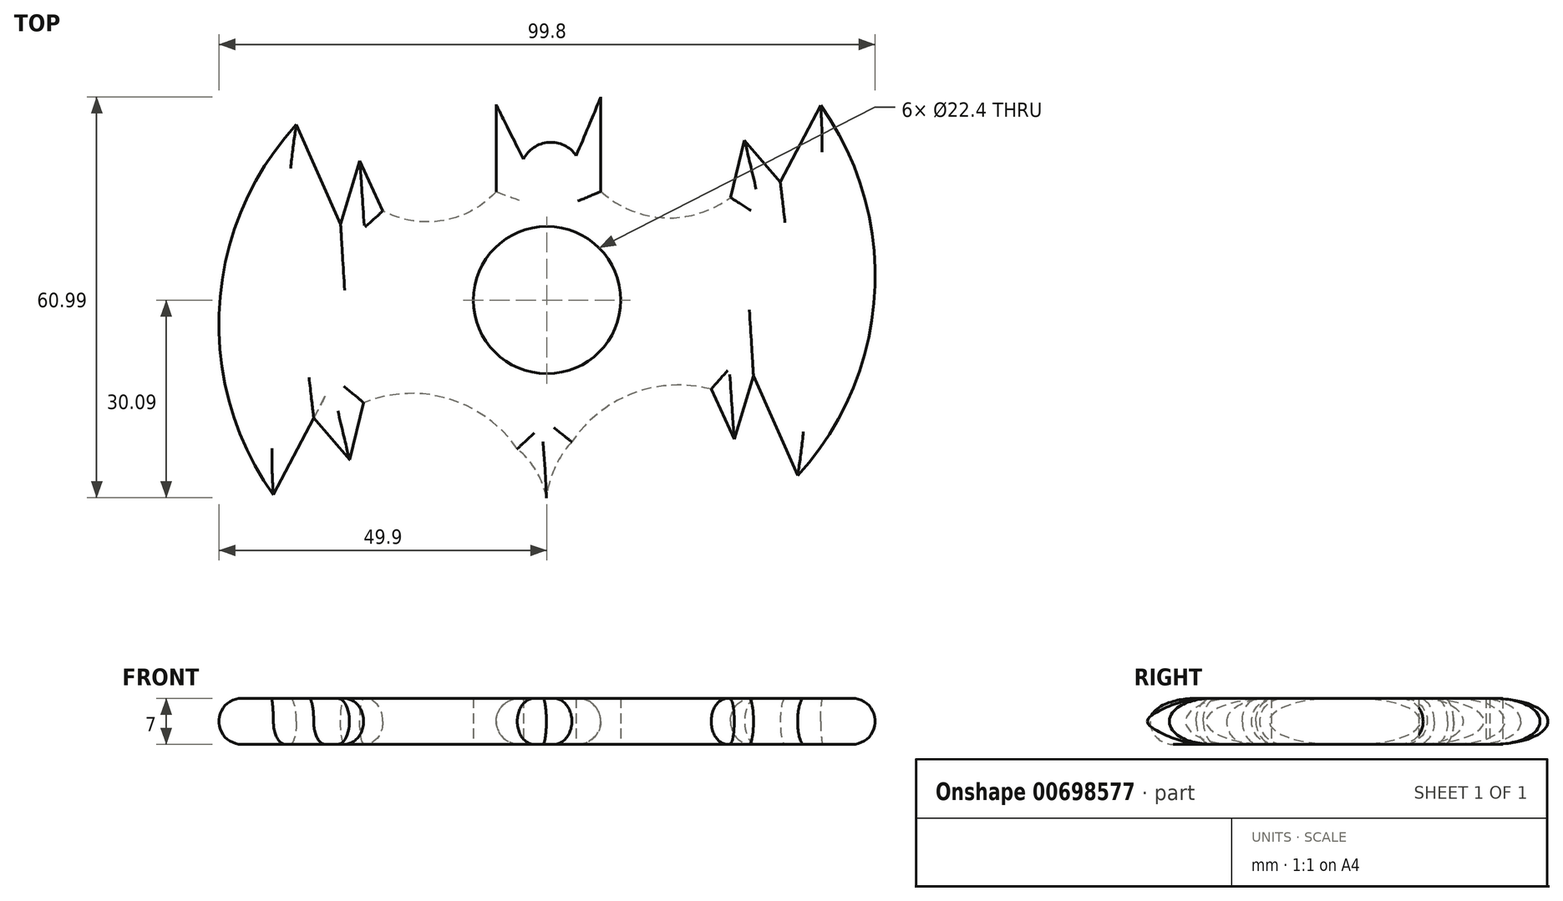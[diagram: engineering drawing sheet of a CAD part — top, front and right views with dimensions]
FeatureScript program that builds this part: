
annotation { "Feature Type Name" : "Feature", "Feature Type Description" : "" }
export const myFeature = defineFeature(function(context is Context, id is Id, definition is map)
    precondition{}
    {
        {
            var Q0;
            Q0=qCreatedBy(makeId("Top.planeOp"),FACE);
            var sketch = newSketch(context, id + "F0", { "sketchPlane" : qUnion([Q0])});
            skCircle(sketch, "E0", {"center": v(0, 0) * mm, "radius": 11.2 * mm});
            skCircle(sketch, "E1", {"center": v(0, 0) * mm, "radius": 13.2 * mm});
            skArc(sketch, "E2", {"start": v(-38.1, 26.72) * mm, "mid": v(-49.82, -0.84) * mm, "end": v(-41.61, -29.64) * mm});
            skArc(sketch, "E3.1.0", {"start": v(38.1, -26.72) * mm, "mid": v(49.82, 0.84) * mm, "end": v(41.61, 29.64) * mm});
            skLineSegment(sketch, "E4", {"start": v(-41.61, -29.64) * mm, "end": v(-35.48, -17.96) * mm});
            skLineSegment(sketch, "E5", {"start": v(-35.48, -17.96) * mm, "end": v(-35.48, -24.97) * mm});
            skArc(sketch, "E6", {"start": v(-4.53, -22.63) * mm, "mid": v(-14.98, -15.03) * mm, "end": v(-27.89, -15.62) * mm});
            skLineSegment(sketch, "E7.1.0", {"start": v(41.61, 29.64) * mm, "end": v(35.48, 17.96) * mm});
            skLineSegment(sketch, "E7.1.1", {"start": v(35.48, 17.96) * mm, "end": v(30.03, 24.29) * mm});
            skLineSegment(sketch, "E7.1.2", {"start": v(30.03, 24.29) * mm, "end": v(27.89, 15.62) * mm});
            skLineSegment(sketch, "E8", {"start": v(38.1, -26.72) * mm, "end": v(31.4, -11.53) * mm});
            skLineSegment(sketch, "E9", {"start": v(31.4, -11.53) * mm, "end": v(28.47, -21.17) * mm});
            skLineSegment(sketch, "E10", {"start": v(28.47, -21.17) * mm, "end": v(24.97, -13.58) * mm});
            skArc(sketch, "E11.1.0", {"start": v(-24.97, 13.58) * mm, "mid": v(-15.85, 12.08) * mm, "end": v(-7.74, 16.5) * mm});
            skLineSegment(sketch, "E11.1.2", {"start": v(-28.47, 21.17) * mm, "end": v(-24.97, 13.58) * mm});
            skLineSegment(sketch, "E11.1.4", {"start": v(-31.4, 11.53) * mm, "end": v(-28.47, 21.17) * mm});
            skLineSegment(sketch, "E11.1.5", {"start": v(-38.1, 26.72) * mm, "end": v(-31.4, 11.53) * mm});
            skArc(sketch, "E12", {"start": v(0, -34.06) * mm, "mid": v(-0.76, -27.75) * mm, "end": v(-4.53, -22.63) * mm});
            skArc(sketch, "E13.1.0", {"start": v(8.2, 16.53) * mm, "mid": v(17.88, 12.52) * mm, "end": v(27.89, 15.62) * mm});
            skLineSegment(sketch, "E14", {"start": v(-7.74, 16.5) * mm, "end": v(-7.74, 29.75) * mm});
            skLineSegment(sketch, "E15", {"start": v(-7.74, 29.75) * mm, "end": v(-3.6, 21.41) * mm});
            skLineSegment(sketch, "E16", {"start": v(8.2, 16.53) * mm, "end": v(8.2, 30.9) * mm});
            skLineSegment(sketch, "E17", {"start": v(8.2, 30.9) * mm, "end": v(4.45, 21.97) * mm});
            skArc(sketch, "E18", {"start": v(4.45, 21.97) * mm, "mid": v(0.27, 24) * mm, "end": v(-3.6, 21.41) * mm});
            skArc(sketch, "E19", {"start": v(24.97, -13.58) * mm, "mid": v(13.1, -14.2) * mm, "end": v(3.78, -21.57) * mm});
            skArc(sketch, "E20", {"start": v(3.78, -21.57) * mm, "mid": v(0.47, -27.38) * mm, "end": v(0, -34.06) * mm});
            skLineSegment(sketch, "E21.1.0", {"start": v(-35.48, -17.96) * mm, "end": v(-30.03, -24.29) * mm});
            skLineSegment(sketch, "E21.1.1", {"start": v(-30.03, -24.29) * mm, "end": v(-27.89, -15.62) * mm});
            skSolve(sketch);
        }
        {
            var Q0;
            Q0=makeQuery(id+"F0.imprint","IMPRINT",FACE,{"disambiguationData":[TD([[makeQuery(id+"F0.imprint","IMPRINT",EDGE,{"derivedFrom":sQuery(id+"F0.wireOp",EDGE,"E0")}),-1.0]])]});
            var Q1;
            Q1=makeQuery(id+"F0.imprint","IMPRINT",FACE,{"disambiguationData":[TD([[makeQuery(id+"F0.imprint","IMPRINT",EDGE,{"derivedFrom":sQuery(id+"F0.wireOp",EDGE,"E1")}),-1.0]])]});
            extrude(context, id + "F1", {"entities" : qUnion([Q0, Q1]), "depth" : 7 * mm, "offsetDistance" : 25 * mm});
        }
        {
            var Q0;
            Q0=makeQuery(id+"F1.opExtrude","CAP_EDGE",EDGE,{"disambiguationData":[OSD([sQuery(id+"F0.wireOp",EDGE,"E20")])],"isStart":false});
            var Q1;
            Q1=makeQuery(id+"F1.opExtrude","CAP_EDGE",EDGE,{"disambiguationData":[OSD([sQuery(id+"F0.wireOp",EDGE,"E19")])],"isStart":false});
            var Q2;
            Q2=makeQuery(id+"F1.opExtrude","CAP_EDGE",EDGE,{"disambiguationData":[OSD([sQuery(id+"F0.wireOp",EDGE,"E9")])],"isStart":false});
            var Q3;
            Q3=makeQuery(id+"F1.opExtrude","CAP_EDGE",EDGE,{"disambiguationData":[OSD([sQuery(id+"F0.wireOp",EDGE,"E3.1.0")])],"isStart":false});
            var Q4;
            Q4=makeQuery(id+"F1.opExtrude","CAP_EDGE",EDGE,{"disambiguationData":[OSD([sQuery(id+"F0.wireOp",EDGE,"E8")])],"isStart":false});
            var Q5;
            Q5=makeQuery(id+"F1.opExtrude","CAP_EDGE",EDGE,{"disambiguationData":[OSD([sQuery(id+"F0.wireOp",EDGE,"E7.1.0")])],"isStart":false});
            var Q6;
            Q6=makeQuery(id+"F1.opExtrude","CAP_EDGE",EDGE,{"disambiguationData":[OSD([sQuery(id+"F0.wireOp",EDGE,"E7.1.1")])],"isStart":false});
            var Q7;
            Q7=makeQuery(id+"F1.opExtrude","CAP_EDGE",EDGE,{"disambiguationData":[OSD([sQuery(id+"F0.wireOp",EDGE,"E7.1.2")])],"isStart":false});
            var Q8;
            Q8=makeQuery(id+"F1.opExtrude","CAP_EDGE",EDGE,{"disambiguationData":[OSD([sQuery(id+"F0.wireOp",EDGE,"E13.1.0")])],"isStart":false});
            var Q9;
            Q9=makeQuery(id+"F1.opExtrude","CAP_EDGE",EDGE,{"disambiguationData":[OSD([sQuery(id+"F0.wireOp",EDGE,"E16")])],"isStart":false});
            var Q10;
            Q10=makeQuery(id+"F1.opExtrude","CAP_EDGE",EDGE,{"disambiguationData":[OSD([sQuery(id+"F0.wireOp",EDGE,"E14")])],"isStart":false});
            var Q11;
            Q11=makeQuery(id+"F1.opExtrude","CAP_EDGE",EDGE,{"disambiguationData":[OSD([sQuery(id+"F0.wireOp",EDGE,"E11.1.0")])],"isStart":false});
            var Q12;
            Q12=makeQuery(id+"F1.opExtrude","CAP_EDGE",EDGE,{"disambiguationData":[OSD([sQuery(id+"F0.wireOp",EDGE,"E11.1.2")])],"isStart":false});
            var Q13;
            Q13=makeQuery(id+"F1.opExtrude","CAP_EDGE",EDGE,{"disambiguationData":[OSD([sQuery(id+"F0.wireOp",EDGE,"E11.1.5")])],"isStart":false});
            var Q14;
            Q14=makeQuery(id+"F1.opExtrude","CAP_EDGE",EDGE,{"disambiguationData":[OSD([sQuery(id+"F0.wireOp",EDGE,"E11.1.4")])],"isStart":false});
            var Q15;
            Q15=makeQuery(id+"F1.opExtrude","CAP_EDGE",EDGE,{"disambiguationData":[OSD([sQuery(id+"F0.wireOp",EDGE,"E2")])],"isStart":false});
            var Q16;
            Q16=makeQuery(id+"F1.opExtrude","CAP_EDGE",EDGE,{"disambiguationData":[OSD([sQuery(id+"F0.wireOp",EDGE,"E4")])],"isStart":false});
            var Q17;
            Q17=makeQuery(id+"F1.opExtrude","CAP_EDGE",EDGE,{"disambiguationData":[OSD([sQuery(id+"F0.wireOp",EDGE,"E12")])],"isStart":false});
            var Q18;
            Q18=makeQuery(id+"F1.opExtrude","CAP_EDGE",EDGE,{"disambiguationData":[OSD([sQuery(id+"F0.wireOp",EDGE,"E10")])],"isStart":false});
            var Q19;
            Q19=makeQuery(id+"F1.opExtrude","CAP_EDGE",EDGE,{"disambiguationData":[OSD([sQuery(id+"F0.wireOp",EDGE,"E21.1.1")])],"isStart":false});
            var Q20;
            Q20=makeQuery(id+"F1.opExtrude","CAP_EDGE",EDGE,{"disambiguationData":[OSD([sQuery(id+"F0.wireOp",EDGE,"E6")])],"isStart":false});
            var Q21;
            Q21=makeQuery(id+"F1.opExtrude","CAP_EDGE",EDGE,{"disambiguationData":[OSD([sQuery(id+"F0.wireOp",EDGE,"E21.1.0")])],"isStart":false});
            var Q22;
            Q22=makeQuery(id+"F1.opExtrude","CAP_EDGE",EDGE,{"disambiguationData":[OSD([sQuery(id+"F0.wireOp",EDGE,"E3.1.0")])],"isStart":true});
            var Q23;
            Q23=makeQuery(id+"F1.opExtrude","CAP_EDGE",EDGE,{"disambiguationData":[OSD([sQuery(id+"F0.wireOp",EDGE,"E8")])],"isStart":true});
            var Q24;
            Q24=makeQuery(id+"F1.opExtrude","CAP_EDGE",EDGE,{"disambiguationData":[OSD([sQuery(id+"F0.wireOp",EDGE,"E9")])],"isStart":true});
            var Q25;
            Q25=makeQuery(id+"F1.opExtrude","CAP_EDGE",EDGE,{"disambiguationData":[OSD([sQuery(id+"F0.wireOp",EDGE,"E10")])],"isStart":true});
            var Q26;
            Q26=makeQuery(id+"F1.opExtrude","CAP_EDGE",EDGE,{"disambiguationData":[OSD([sQuery(id+"F0.wireOp",EDGE,"E19")])],"isStart":true});
            var Q27;
            Q27=makeQuery(id+"F1.opExtrude","CAP_EDGE",EDGE,{"disambiguationData":[OSD([sQuery(id+"F0.wireOp",EDGE,"E6")])],"isStart":true});
            var Q28;
            Q28=makeQuery(id+"F1.opExtrude","CAP_EDGE",EDGE,{"disambiguationData":[OSD([sQuery(id+"F0.wireOp",EDGE,"E12")])],"isStart":true});
            var Q29;
            Q29=makeQuery(id+"F1.opExtrude","CAP_EDGE",EDGE,{"disambiguationData":[OSD([sQuery(id+"F0.wireOp",EDGE,"E20")])],"isStart":true});
            var Q30;
            Q30=makeQuery(id+"F1.opExtrude","CAP_EDGE",EDGE,{"disambiguationData":[OSD([sQuery(id+"F0.wireOp",EDGE,"E21.1.1")])],"isStart":true});
            var Q31;
            Q31=makeQuery(id+"F1.opExtrude","CAP_EDGE",EDGE,{"disambiguationData":[OSD([sQuery(id+"F0.wireOp",EDGE,"E21.1.0")])],"isStart":true});
            var Q32;
            Q32=makeQuery(id+"F1.opExtrude","CAP_EDGE",EDGE,{"disambiguationData":[OSD([sQuery(id+"F0.wireOp",EDGE,"E11.1.5")])],"isStart":true});
            var Q33;
            Q33=makeQuery(id+"F1.opExtrude","CAP_EDGE",EDGE,{"disambiguationData":[OSD([sQuery(id+"F0.wireOp",EDGE,"E11.1.4")])],"isStart":true});
            var Q34;
            Q34=makeQuery(id+"F1.opExtrude","CAP_EDGE",EDGE,{"disambiguationData":[OSD([sQuery(id+"F0.wireOp",EDGE,"E14")])],"isStart":true});
            var Q35;
            Q35=makeQuery(id+"F1.opExtrude","CAP_EDGE",EDGE,{"disambiguationData":[OSD([sQuery(id+"F0.wireOp",EDGE,"E16")])],"isStart":true});
            var Q36;
            Q36=makeQuery(id+"F1.opExtrude","CAP_EDGE",EDGE,{"disambiguationData":[OSD([sQuery(id+"F0.wireOp",EDGE,"E13.1.0")])],"isStart":true});
            var Q37;
            Q37=makeQuery(id+"F1.opExtrude","CAP_EDGE",EDGE,{"disambiguationData":[OSD([sQuery(id+"F0.wireOp",EDGE,"E7.1.2")])],"isStart":true});
            var Q38;
            Q38=makeQuery(id+"F1.opExtrude","CAP_EDGE",EDGE,{"disambiguationData":[OSD([sQuery(id+"F0.wireOp",EDGE,"E7.1.1")])],"isStart":true});
            var Q39;
            Q39=makeQuery(id+"F1.opExtrude","CAP_EDGE",EDGE,{"disambiguationData":[OSD([sQuery(id+"F0.wireOp",EDGE,"E7.1.0")])],"isStart":true});
            var Q40;
            Q40=makeQuery(id+"F1.opExtrude","CAP_EDGE",EDGE,{"disambiguationData":[OSD([sQuery(id+"F0.wireOp",EDGE,"E11.1.0")])],"isStart":true});
            var Q41;
            Q41=makeQuery(id+"F1.opExtrude","CAP_EDGE",EDGE,{"disambiguationData":[OSD([sQuery(id+"F0.wireOp",EDGE,"E11.1.2")])],"isStart":true});
            var Q42;
            Q42=makeQuery(id+"F1.opExtrude","CAP_EDGE",EDGE,{"disambiguationData":[OSD([sQuery(id+"F0.wireOp",EDGE,"E2")])],"isStart":true});
            fillet(context, id + "F2", {"entities" : qUnion([Q0, Q1, Q2, Q3, Q4, Q5, Q6, Q7, Q8, Q9, Q10, Q11, Q12, Q13, Q14, Q15, Q16, Q17, Q18, Q19, Q20, Q21, Q22, Q23, Q24, Q25, Q26, Q27, Q28, Q29, Q30, Q31, Q32, Q33, Q34, Q35, Q36, Q37, Q38, Q39, Q40, Q41, Q42]), "radius" : 3.5 * mm, "tangentPropagation" : true, "allowEdgeOverflow" : false});
        }
    });
